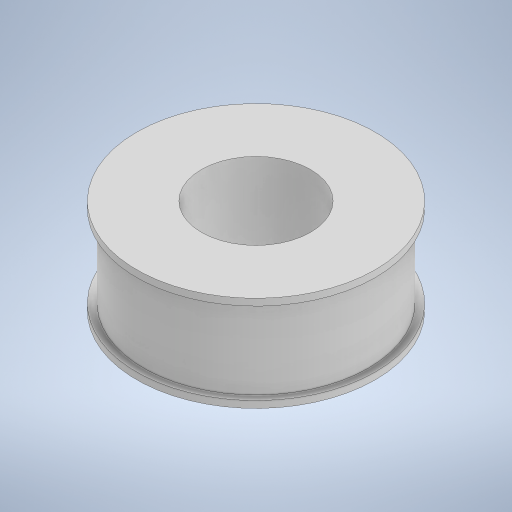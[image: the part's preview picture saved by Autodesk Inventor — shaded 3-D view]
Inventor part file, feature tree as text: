
AUTODESK INVENTOR PART (.ipt)
format: ipt  version: 2023 (Build 270158000, 158)  size: 243,712 bytes
history: native  units: mm
features: sketch x2, other x1, extrude x1, revolve x1
ambient origin geometry x8: Origin, YZ Plane, XZ Plane, XY Plane, X Axis, Y Axis, Z Axis, Center Point
bodies: Body1 (feature_tree)
feature tree (5):
  other  "Твердое тело1"
  extrude  "Выдавливание1"  Depth=16.0mm
  revolve  "Вращение1"
  sketch  "Эскиз1"
  sketch  "Эскиз2"
